# Revit family: Magnuson-Oxi_Bistrot-Square_Table-1
name_source: partatom
category: Furniture
revit_build: Autodesk Revit 2016 (Build: 20150220_1215(x64)
units: mm (PartAtom-declared; Revit-internal decimal feet)

## family parameters
Always vertical = Yes
Cut with Voids When Loaded = No
OmniClass Number = 23.40.20.00
OmniClass Title = General Furniture and Specialties
Room Calculation Point = No
Shared = No
Work Plane-Based = No

## types (1)
- OXI-30
    Assembly Code = E2020200
    Base Finish = MAG-Metal Paint Black
    Depth = 27 1/2"
    Description = Outdoor Table Square  27 1/2"D x 27 1/2"W x 29 1/8"H
    Edge Finish = MAG-Phenolic
    Glide Finish = MAG-Plastic Black
    Height = 29 1/8"
    Keynote = 12500
    Leg Finish = MAG-Metal Paint Black
    Low Emitting Finish = Yes
    Low Emitting Material = Yes
    Manufacturer = Magnuson Group
    Model = OXI-30
    Percentage of Recycled Content = 0
    Revit File Built By = https://servex-us.com
    Salvage or Reuse = No
    Support Finish = MAG-Metal Paint Black
    Top Finish = MAG-Phenolic
    Type Comments = Outdoor Tables
    URL = www.magnusongroup.com
    Width = 27 1/2"

## geometry (parser evidence)
native form markers: Sweep x5
no freeform markers — native parametric forms only
